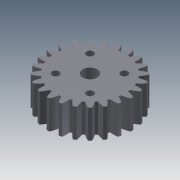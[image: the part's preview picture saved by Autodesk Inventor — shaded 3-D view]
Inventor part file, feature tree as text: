
AUTODESK INVENTOR PART (.ipt)
format: ipt  version: 2015 (Build 190159000, 159)  size: 230,912 bytes
history: native  units: mm (DEFAULTED — no unit token found)
features: plane x3, other x3, sketch x3, extrude x2
ambient origin geometry x8: Origin, YZ Plane, XZ Plane, XY Plane, X Axis, Y Axis, Z Axis, Center Point
bodies: Solid1 (feature_tree)
feature tree (11):
  extrude  "Extrusion1"  Depth=20.0mm TaperAngle=0.0deg
  plane  "Work Plane2"
  plane  "Work Plane8"
  plane  "Work Plane9"
  other  "Spur Gear"
  extrude  "Extrusion3"  Depth=10.0mm TaperAngle=0.0deg
  sketch  "Sketch1"  dims[d0=58.493319mm d1=20.0mm d2=0.0mm]
  sketch  "Sketch2"  dims[d3=54.193548mm d4=10.0mm d5=0.0mm]
  other  "Srf1"
  sketch  "Sketch3"  dims[d16=70.0mm d17=0.0mm d34=1.308997mm d39=0.0mm d41=0.0mm d43=70.0mm d46=70.0mm d47=0.0mm d48=0.0mm d49=10.0mm d52=5.0mm d53=12.0mm d54=12.0mm d55=10.0mm d56=0.0mm]
  other  "Pitch Diameter"
